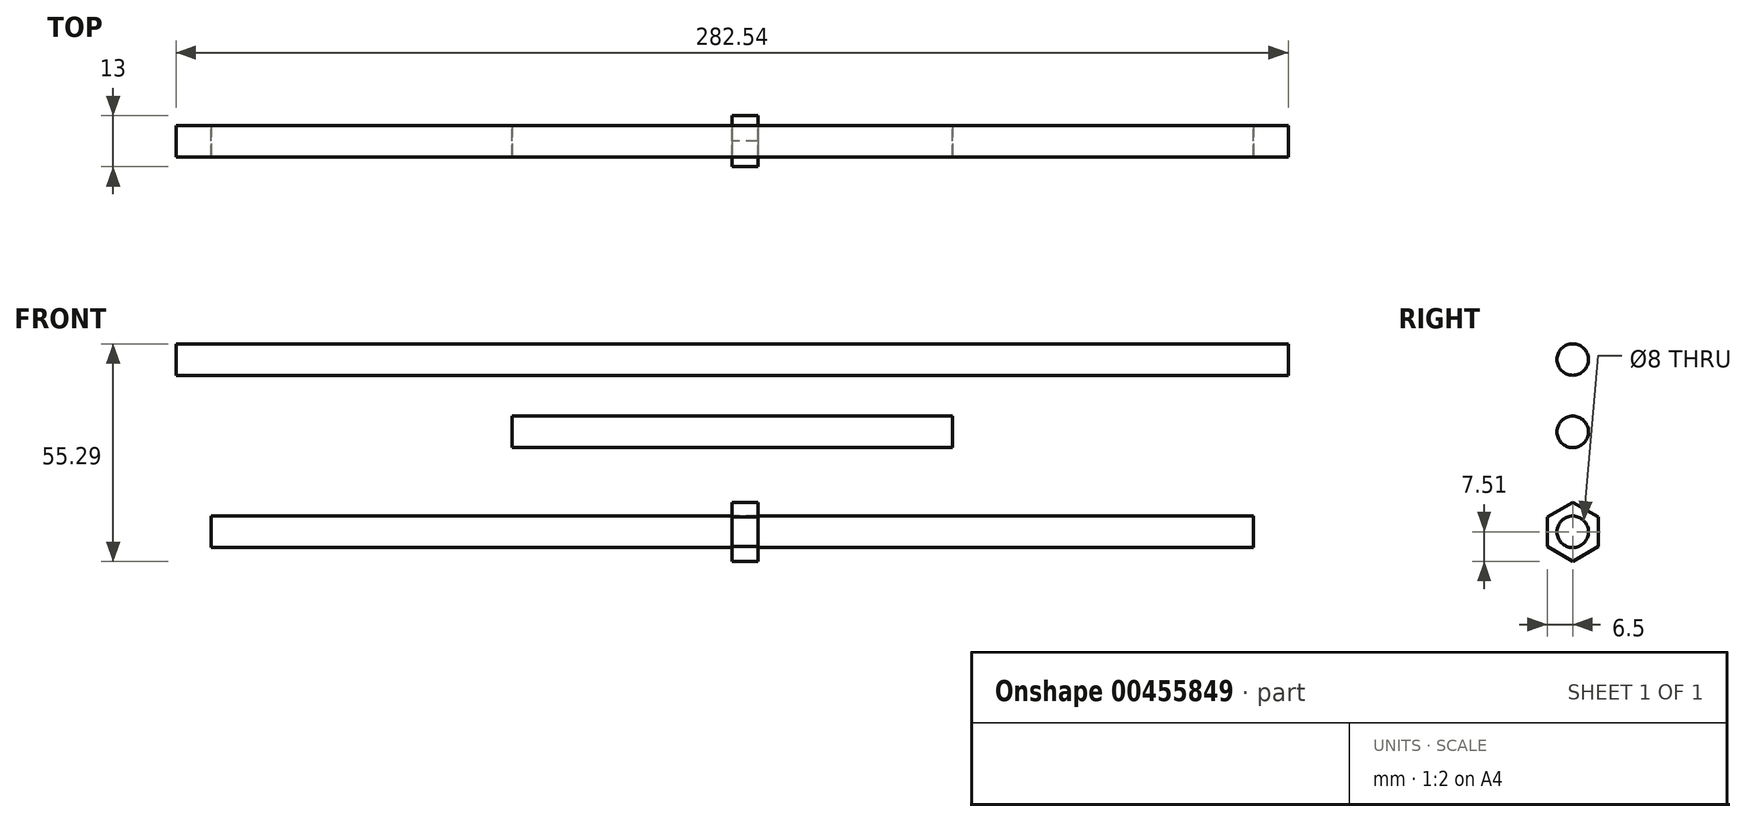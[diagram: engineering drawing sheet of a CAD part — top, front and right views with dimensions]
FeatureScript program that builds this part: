
annotation { "Feature Type Name" : "Feature", "Feature Type Description" : "" }
export const myFeature = defineFeature(function(context is Context, id is Id, definition is map)
    precondition{}
    {
        {
            var Q0;
            Q0=qCreatedBy(makeId("Front.planeOp"),FACE);
            var sketch = newSketch(context, id + "F0", { "sketchPlane" : qUnion([Q0])});
            skLineSegment(sketch, "E0", {"start": v(-132.41, 0) * mm, "end": v(132.41, 0) * mm, "construction": true});
            skLineSegment(sketch, "E1", {"start": v(132.41, 4) * mm, "end": v(132.41, -4) * mm, "construction": true});
            skLineSegment(sketch, "E2", {"start": v(-132.41, 4) * mm, "end": v(-132.41, -4) * mm, "construction": true});
            skSolve(sketch);
        }
        {
            var Q0;
            Q0=qCreatedBy(makeId("Right.planeOp"),FACE);
            var sketch = newSketch(context, id + "F1", { "sketchPlane" : qUnion([Q0])});
            skCircle(sketch, "E3", {"center": v(0, 0) * mm, "radius": 4 * mm});
            skCircle(sketch, "E4.cCircle", {"center": v(0, 0) * mm, "radius": 6.5 * mm, "construction": true});
            skLineSegment(sketch, "E4.0", {"start": v(0, 7.5) * mm, "end": v(6.5, 3.75) * mm});
            skLineSegment(sketch, "E4.1", {"start": v(6.5, 3.75) * mm, "end": v(6.5, -3.75) * mm});
            skLineSegment(sketch, "E4.2", {"start": v(6.5, -3.75) * mm, "end": v(0, -7.5) * mm});
            skLineSegment(sketch, "E4.3", {"start": v(0, -7.5) * mm, "end": v(-6.5, -3.75) * mm});
            skLineSegment(sketch, "E4.4", {"start": v(-6.5, -3.75) * mm, "end": v(-6.5, 3.75) * mm});
            skLineSegment(sketch, "E4.5", {"start": v(-6.5, 3.75) * mm, "end": v(0, 7.5) * mm});
            skPoint(sketch, "E4.0.midPoint", {"position": v(3.25, 5.63) * mm});
            skSolve(sketch);
        }
        {
            var Q0;
            Q0=makeQuery(id+"F1.imprint","IMPRINT",FACE,{"disambiguationData":[TD([[makeQuery(id+"F1.imprint","IMPRINT",EDGE,{"derivedFrom":sQuery(id+"F1.wireOp",EDGE,"E3")}),1.0]])]});
            var Q1;
            Q1=sQuery(id+"F0.wireOp",VERTEX,"E0.end");
            var Q2;
            Q2=sQuery(id+"F0.wireOp",VERTEX,"E0.start");
            extrude(context, id + "F2", {"entities" : qUnion([Q0]), "endBound" : BoundingType.UP_TO_VERTEX, "endBoundEntityVertex" : qUnion([Q1]), "depth" : 25.4 * mm, "hasSecondDirection" : true, "secondDirectionBound" : BoundingType.UP_TO_VERTEX, "secondDirectionOppositeDirection" : true, "secondDirectionBoundEntityVertex" : qUnion([Q2]), "secondDirectionDepth" : 25.4 * mm});
        }
        {
            var Q0;
            Q0 = qSketchRegion(id + "F1", true);
            extrude(context, id + "F3", {"entities" : qUnion([Q0]), "depth" : 6.5 * mm});
        }
        {
            var Q0;
            Q0=qCreatedBy(makeId("Front.planeOp"),FACE);
            var sketch = newSketch(context, id + "F4", { "sketchPlane" : qUnion([Q0])});
            skLineSegment(sketch, "E5", {"start": v(-55.93, 25.4) * mm, "end": v(55.93, 25.4) * mm, "construction": true});
            skLineSegment(sketch, "E6", {"start": v(0, 0) * mm, "end": v(0, 58.06) * mm, "construction": true});
            skPoint(sketch, "E7", {"position": v(0, 25.4) * mm});
            skSolve(sketch);
        }
        {
            var Q0;
            Q0=qCreatedBy(makeId("Right.planeOp"),FACE);
            var sketch = newSketch(context, id + "F5", { "sketchPlane" : qUnion([Q0])});
            skCircle(sketch, "E8", {"center": v(0, 25.4) * mm, "radius": 4 * mm});
            skSolve(sketch);
        }
        {
            var Q0;
            Q0 = qSketchRegion(id + "F5", true);
            var Q1;
            Q1=sQuery(id+"F4.wireOp",VERTEX,"E5.end");
            var Q2;
            Q2=sQuery(id+"F4.wireOp",VERTEX,"E5.start");
            extrude(context, id + "F6", {"entities" : qUnion([Q0]), "endBound" : BoundingType.UP_TO_VERTEX, "endBoundEntityVertex" : qUnion([Q1]), "depth" : 25.4 * mm, "hasSecondDirection" : true, "secondDirectionBound" : BoundingType.UP_TO_VERTEX, "secondDirectionOppositeDirection" : true, "secondDirectionBoundEntityVertex" : qUnion([Q2]), "secondDirectionDepth" : 25.4 * mm});
        }
        {
            var Q0;
            Q0=qCreatedBy(makeId("Front.planeOp"),FACE);
            var sketch = newSketch(context, id + "F7", { "sketchPlane" : qUnion([Q0])});
            skLineSegment(sketch, "E9", {"start": v(-141.27, 43.78) * mm, "end": v(141.27, 43.78) * mm, "construction": true});
            skPoint(sketch, "E10", {"position": v(0, 43.78) * mm});
            skSolve(sketch);
        }
        {
            var Q0;
            Q0=qCreatedBy(makeId("Right.planeOp"),FACE);
            var sketch = newSketch(context, id + "F8", { "sketchPlane" : qUnion([Q0])});
            skCircle(sketch, "E11", {"center": v(0, 43.78) * mm, "radius": 4 * mm});
            skSolve(sketch);
        }
        {
            var Q0;
            Q0=makeQuery(id+"F8.imprint","IMPRINT",FACE,{"disambiguationData":[TD([[makeQuery(id+"F8.imprint","IMPRINT",EDGE,{"derivedFrom":sQuery(id+"F8.wireOp",EDGE,"E11")}),1.0]])]});
            var Q1;
            Q1=sQuery(id+"F7.wireOp",VERTEX,"E9.end");
            var Q2;
            Q2=sQuery(id+"F7.wireOp",VERTEX,"E9.start");
            extrude(context, id + "F9", {"entities" : qUnion([Q0]), "endBound" : BoundingType.UP_TO_VERTEX, "depth" : 25.4 * mm, "endBoundEntityVertex" : qUnion([Q1]), "offsetDistance" : 25.4 * mm, "hasSecondDirection" : true, "secondDirectionBound" : BoundingType.UP_TO_VERTEX, "secondDirectionOppositeDirection" : true, "secondDirectionDepth" : 25.4 * mm, "secondDirectionBoundEntityVertex" : qUnion([Q2])});
        }
    });
